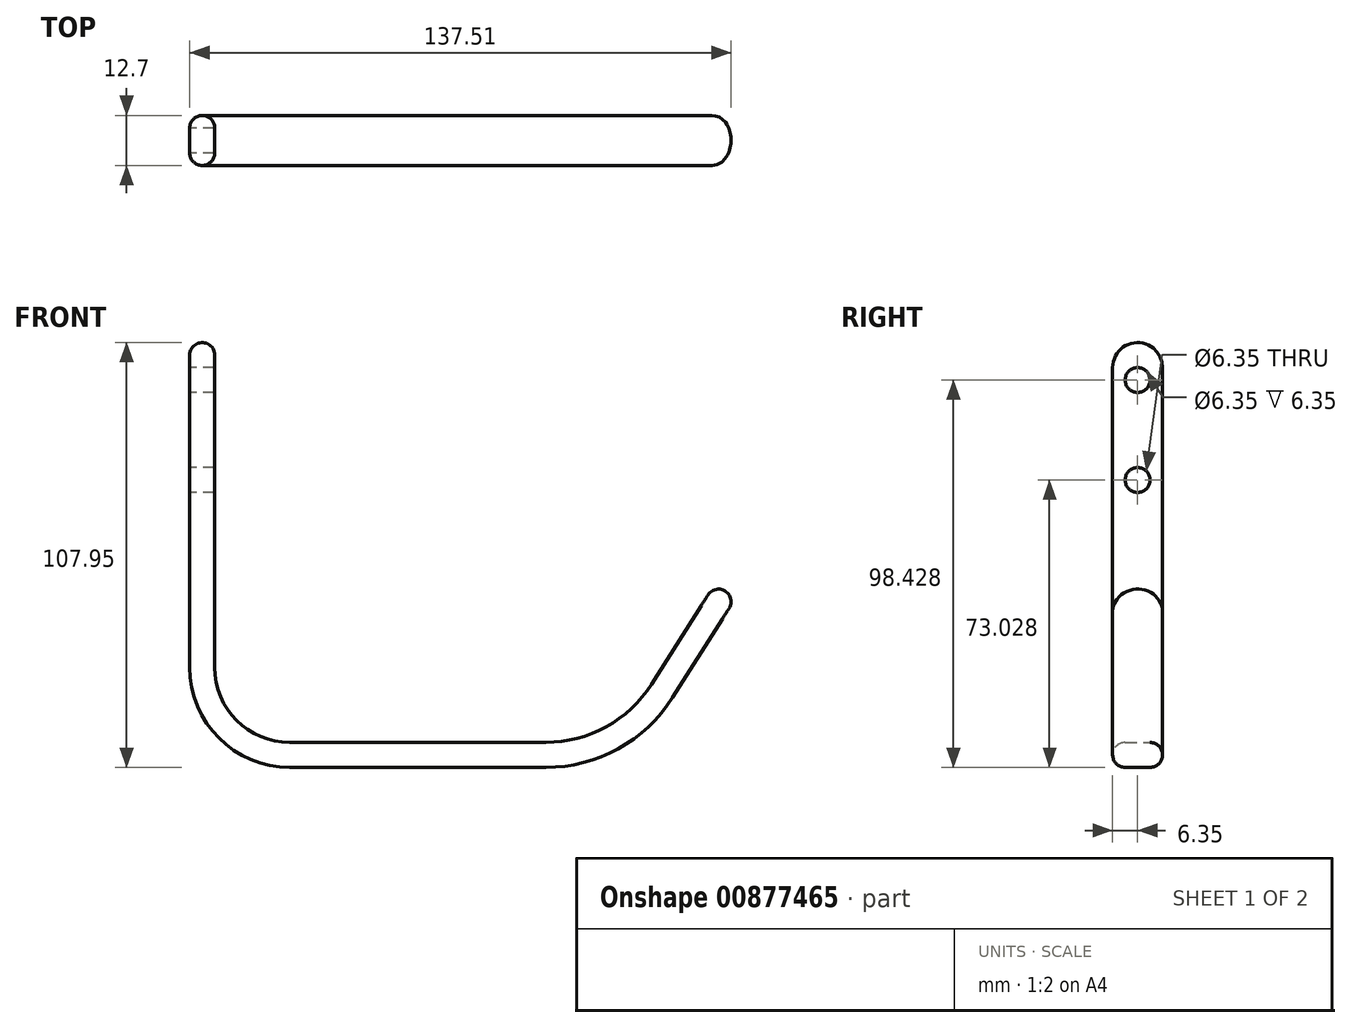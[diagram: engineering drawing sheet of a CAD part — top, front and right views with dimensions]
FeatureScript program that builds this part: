
annotation { "Feature Type Name" : "Feature", "Feature Type Description" : "" }
export const myFeature = defineFeature(function(context is Context, id is Id, definition is map)
    precondition{}
    {
        {
            var Q0;
            Q0=qCreatedBy(makeId("Front.planeOp"),FACE);
            var sketch = newSketch(context, id + "F0", { "sketchPlane" : qUnion([Q0])});
            skLineSegment(sketch, "E0", {"start": v(-81.18, 75.32) * mm, "end": v(-81.18, -7.23) * mm});
            skLineSegment(sketch, "E1", {"start": v(-62.13, -26.28) * mm, "end": v(2.94, -26.28) * mm});
            skLineSegment(sketch, "E2", {"start": v(29.77, -11.5) * mm, "end": v(45.82, 13.88) * mm});
            skPoint(sketch, "E3.visualSharp", {"position": v(20.42, -26.28) * mm});
            skArc(sketch, "E3.filletArc", {"start": v(2.94, -26.28) * mm, "mid": v(18.25, -22.34) * mm, "end": v(29.77, -11.5) * mm});
            skPoint(sketch, "E4.visualSharp", {"position": v(-81.18, -26.28) * mm});
            skArc(sketch, "E4.filletArc", {"start": v(-81.18, -7.23) * mm, "mid": v(-75.6, -20.7) * mm, "end": v(-62.13, -26.28) * mm});
            skLineSegment(sketch, "E5.0", {"start": v(-87.53, 75.32) * mm, "end": v(-87.53, -7.23) * mm});
            skLineSegment(sketch, "E6.0", {"start": v(-62.13, -32.63) * mm, "end": v(2.94, -32.63) * mm});
            skLineSegment(sketch, "E7.0", {"start": v(35.14, -14.9) * mm, "end": v(51.19, 10.49) * mm});
            skArc(sketch, "E8.0", {"start": v(2.94, -32.63) * mm, "mid": v(21.32, -27.9) * mm, "end": v(35.14, -14.9) * mm});
            skArc(sketch, "E9.0", {"start": v(-87.53, -7.23) * mm, "mid": v(-80.09, -25.19) * mm, "end": v(-62.13, -32.63) * mm});
            skLineSegment(sketch, "E10", {"start": v(-87.53, 75.32) * mm, "end": v(-81.18, 75.32) * mm});
            skLineSegment(sketch, "E11", {"start": v(45.82, 13.88) * mm, "end": v(51.19, 10.49) * mm});
            skSolve(sketch);
        }
        {
            var Q0;
            Q0 = qSketchRegion(id + "F0", true);
            extrude(context, id + "F1", {"entities" : qUnion([Q0]), "endBound" : BoundingType.SYMMETRIC, "depth" : 12.7 * mm, "offsetDistance" : 25.4 * mm});
        }
        {
            var Q0;
            Q0=makeQuery(id+"F1.opExtrude","CAP_EDGE",EDGE,{"disambiguationData":[OSD([sQuery(id+"F0.wireOp",EDGE,"E10")])],"isStart":true});
            var Q1;
            Q1=makeQuery(id+"F1.opExtrude","CAP_EDGE",EDGE,{"disambiguationData":[OSD([sQuery(id+"F0.wireOp",EDGE,"E10")])],"isStart":false});
            fillet(context, id + "F2", {"entities" : qUnion([Q0, Q1]), "radius" : 6.35 * mm, "tangentPropagation" : true, "allowEdgeOverflow" : false});
        }
        {
            var Q0;
            Q0=makeQuery(id+"F1.opExtrude","CAP_EDGE",EDGE,{"disambiguationData":[OSD([sQuery(id+"F0.wireOp",EDGE,"E11")])],"isStart":false});
            var Q1;
            Q1=makeQuery(id+"F1.opExtrude","CAP_EDGE",EDGE,{"disambiguationData":[OSD([sQuery(id+"F0.wireOp",EDGE,"E11")])],"isStart":true});
            fillet(context, id + "F3", {"entities" : qUnion([Q0, Q1]), "radius" : 6.35 * mm, "tangentPropagation" : true, "allowEdgeOverflow" : false});
        }
        {
            var Q0;
            Q0=makeQuery(id+"F1.opExtrude","CAP_EDGE",EDGE,{"disambiguationData":[OSD([sQuery(id+"F0.wireOp",EDGE,"E5.0")])],"isStart":false});
            fillet(context, id + "F4", {"entities" : qUnion([Q0]), "radius" : 3.17 * mm, "tangentPropagation" : true, "allowEdgeOverflow" : false});
        }
        {
            var Q0;
            Q0=makeQuery(id+"F1.opExtrude","CAP_EDGE",EDGE,{"disambiguationData":[OSD([sQuery(id+"F0.wireOp",EDGE,"E0")])],"isStart":false});
            fillet(context, id + "F5", {"entities" : qUnion([Q0]), "radius" : 3.17 * mm, "tangentPropagation" : true, "allowEdgeOverflow" : false});
        }
        {
            var Q0;
            Q0=makeQuery(id+"F1.opExtrude","SWEPT_FACE",FACE,{"disambiguationData":[OSD([sQuery(id+"F0.wireOp",EDGE,"E5.0")])]});
            var sketch = newSketch(context, id + "F6", { "sketchPlane" : qUnion([Q0])});
            skLineSegment(sketch, "E12", {"start": v(0, 72.15) * mm, "end": v(0, 65.8) * mm, "construction": true});
            skLineSegment(sketch, "E13", {"start": v(0, 65.8) * mm, "end": v(0, 40.4) * mm, "construction": true});
            skCircle(sketch, "E14", {"center": v(0, 65.8) * mm, "radius": 3.18 * mm});
            skCircle(sketch, "E15", {"center": v(0, 40.4) * mm, "radius": 3.18 * mm});
            skSolve(sketch);
        }
        {
            var Q0;
            Q0 = qSketchRegion(id + "F6", true);
            extrude(context, id + "F7", {"entities" : qUnion([Q0]), "operationType" : NewBodyOperationType.REMOVE, "oppositeDirection" : true, "depth" : 25.4 * mm, "offsetDistance" : 25.4 * mm});
        }
    });
